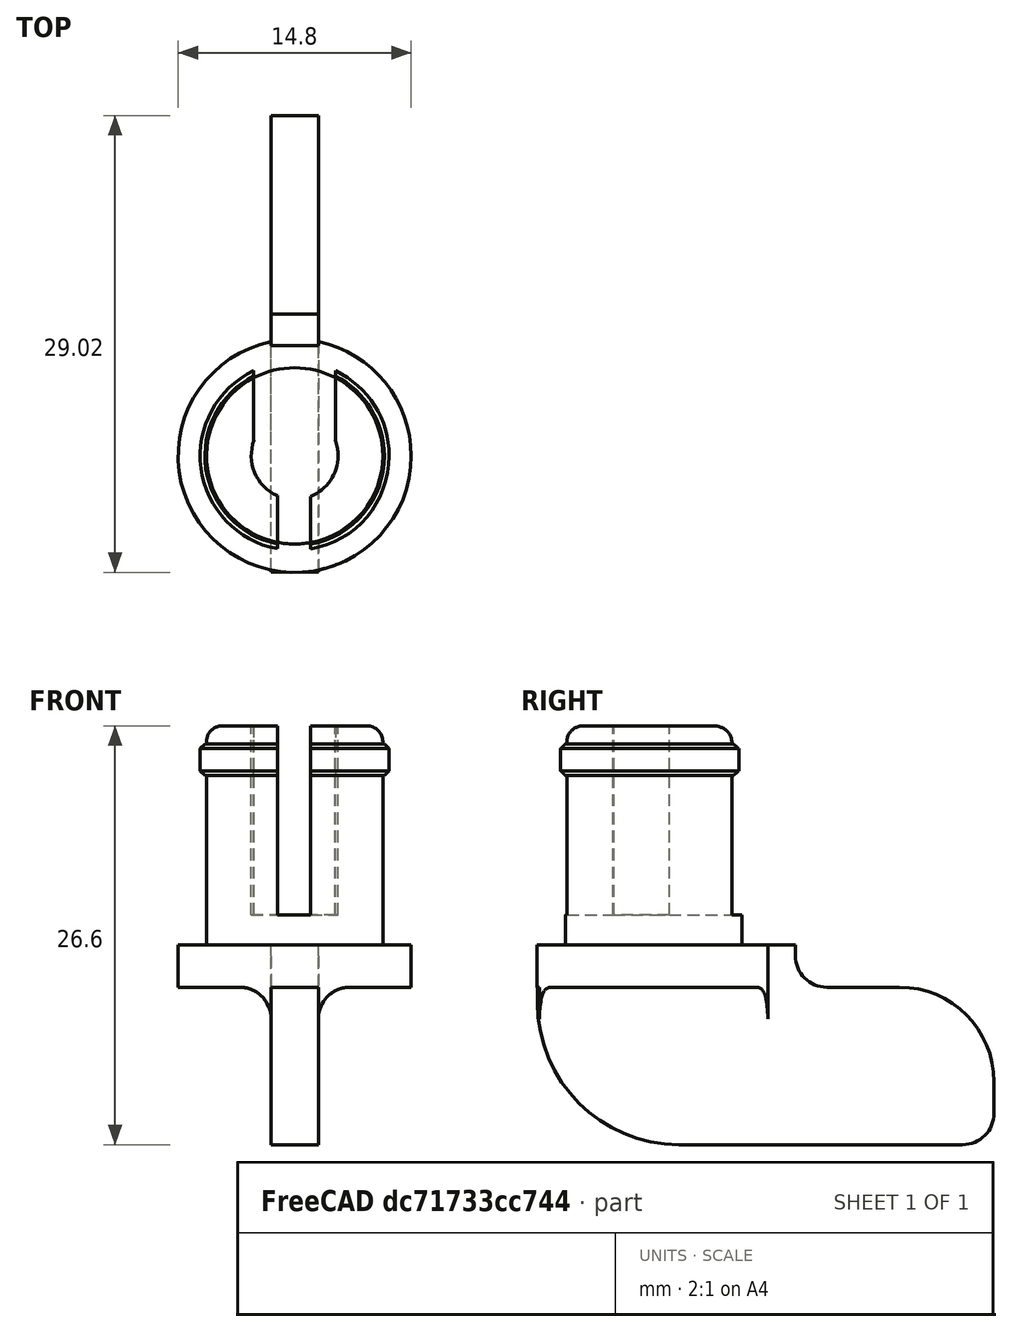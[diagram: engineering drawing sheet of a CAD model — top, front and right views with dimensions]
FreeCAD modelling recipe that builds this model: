
FCSTD DOCUMENT  (FreeCAD 0.16R)
Label: cierre_trasportin_gato
License: All rights reserved
LicenseURL: http://en.wikipedia.org/wiki/All_rights_reserved
objects: Part::Cylinder×4, Part::Box×4, Part::Fillet×4, Part::MultiFuse×4, Part::Cut×1, Part::Chamfer×1
note: 18 computed .brp shape members not serialized (recipe doc carries the construction recipe); baked Part::Feature solids carry a one-line shape summary decoded from their .brp

FEATURE [Part::Cylinder] Cylinder  label="cilindro central"
  Angle = 360
  Height = 16.6
  Radius = 5.6
  expr: Radius = 11.2 / 2
FEATURE [Part::Cylinder] Cylinder001  label="base"
  Angle = 360
  Height = 2.68
  Radius = 7.4
  expr: Radius = 14.8 / 2
FEATURE [Part::Cylinder] Cylinder002  label="cilindro redondo 1"
  Angle = 360
  Height = 2
  Placement = pos=(0,0,13.45) rot=(0,0,1;0rad)
  Radius = 6
  expr: Radius = 12 / 2
FEATURE [Part::Cylinder] Cylinder003  label="central vaciado"
  Angle = 360
  Height = 13.6
  Placement = pos=(0,0,4.6) rot=(0,0,1;0rad)
  Radius = 2.76
  expr: Radius = 5.52 / 2
FEATURE [Part::Box] Box  label="central vaciado 2"
  Height = 13
  Length = 5.2
  Placement = pos=(-2.6,1,4.6) rot=(0,0,1;0rad)
  Width = 5
FEATURE [Part::Box] Box001  label="palometa"
  Height = 10
  Length = 3
  Placement = pos=(-1.5,-7.38,-10) rot=(0,0,1;0rad)
  Width = 29
FEATURE [Part::Fillet] Fillet
  Base = -> Box001
  Edges = 3 edges: [Edge9 r=9,Edge11 r=2,Edge12 r=6]
FEATURE [Part::MultiFuse] Fusion
  Shapes = -> [Cylinder,Cylinder002,Cylinder001]
FEATURE [Part::Box] Box002  label="union palometa"
  Height = 4
  Length = 3
  Placement = pos=(-1.5,7,-1.3) rot=(0,0,1;0rad)
  Width = 2
FEATURE [Part::MultiFuse] Fusion002
  Shapes = -> [Fillet,Box002]
FEATURE [Part::Fillet] Fillet001
  Base = -> Fusion002
  Edges = 1 edges r=2: [Edge7]
FEATURE [Part::Box] Box003  label="central vaciado 003"
  Height = 13
  Length = 2.1
  Placement = pos=(-1.1,-7,4.6) rot=(0,0,1;0rad)
  Width = 5
FEATURE [Part::MultiFuse] Fusion001
  Shapes = -> [Cylinder003,Box,Box003]
FEATURE [Part::Cut] Cut
  Base = -> Fusion
  Tool = -> Fusion001
FEATURE [Part::MultiFuse] Fusion003
  Shapes = -> [Fillet001,Cut]
FEATURE [Part::Fillet] Fillet002
  Base = -> Fusion003
  Edges = 2 edges r=2: [Edge13,Edge26]
FEATURE [Part::Fillet] Fillet003
  Base = -> Fillet002
  Edges = 3 edges r=1: [Edge114,Edge117,Edge123]
FEATURE [Part::Chamfer] Chamfer
  Base = -> Fillet003
  Edges = 4 edges r=0.3: [Edge33,Edge46,Edge72,Edge76]
